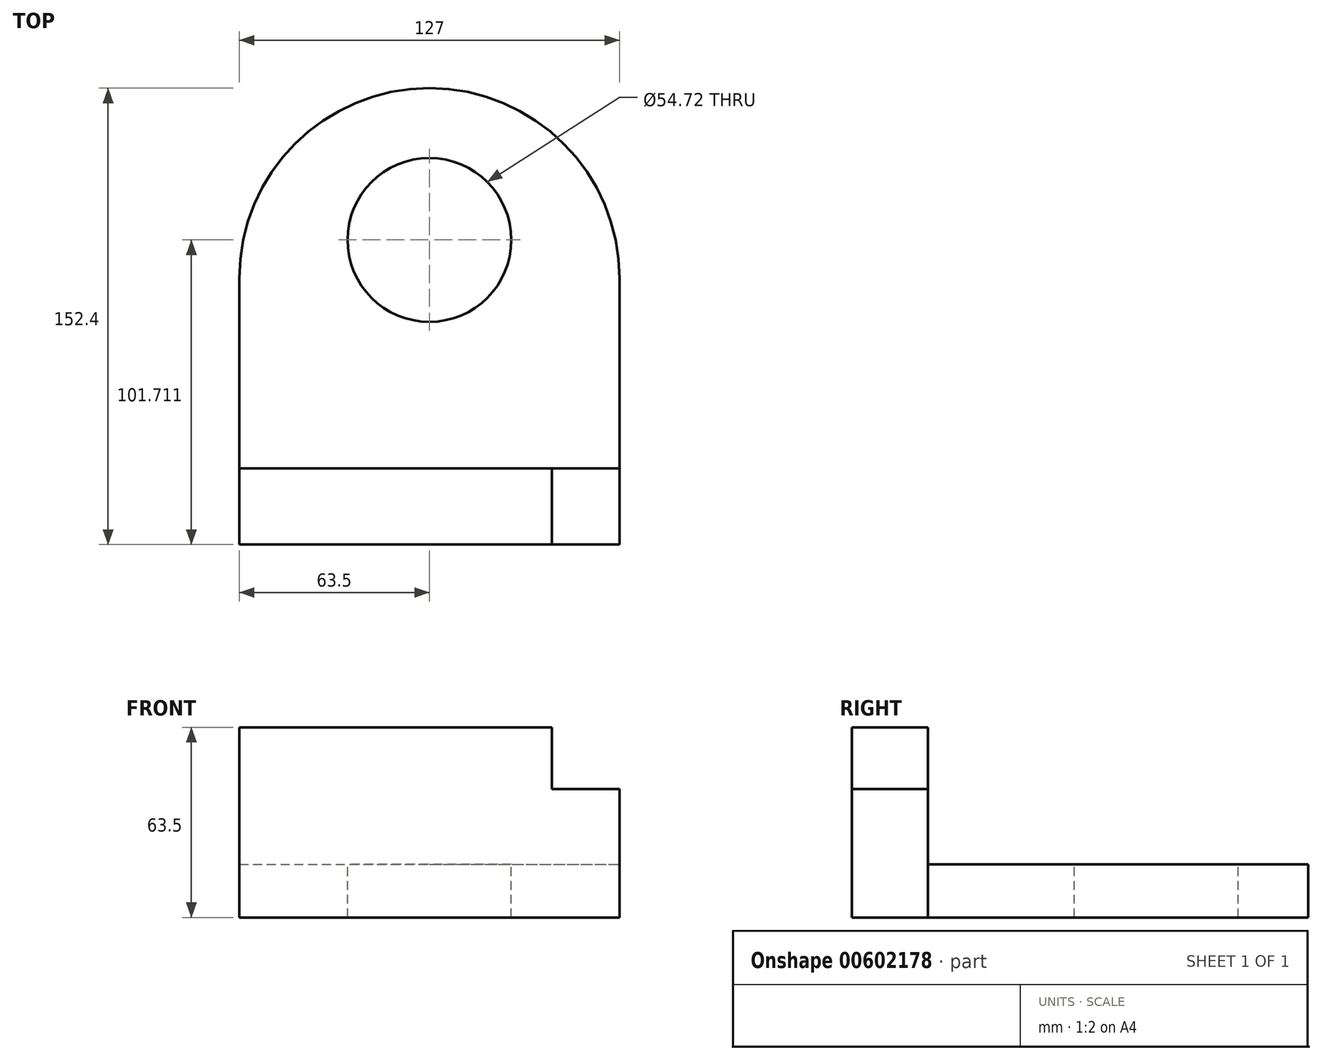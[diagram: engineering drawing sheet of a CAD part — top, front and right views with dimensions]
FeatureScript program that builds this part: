
annotation { "Feature Type Name" : "Feature", "Feature Type Description" : "" }
export const myFeature = defineFeature(function(context is Context, id is Id, definition is map)
    precondition{}
    {
        {
            var Q0;
            Q0=qCreatedBy(makeId("Front.planeOp"),FACE);
            var sketch = newSketch(context, id + "F0", { "sketchPlane" : qUnion([Q0])});
            skLineSegment(sketch, "E0.bottom", {"start": v(-63.5, 31.75) * mm, "end": v(63.5, 31.75) * mm});
            skLineSegment(sketch, "E0.top", {"start": v(-63.5, -31.75) * mm, "end": v(63.5, -31.75) * mm});
            skLineSegment(sketch, "E0.left", {"start": v(-63.5, 31.75) * mm, "end": v(-63.5, -31.75) * mm});
            skLineSegment(sketch, "E0.right", {"start": v(63.5, 31.75) * mm, "end": v(63.5, -31.75) * mm});
            skPoint(sketch, "E0.middle", {"position": v(0, 0) * mm});
            skSolve(sketch);
        }
        {
            var Q0;
            Q0=makeQuery(id+"F0.imprint","IMPRINT",FACE,{"disambiguationData":[TD([[makeQuery(id+"F0.imprint","IMPRINT",EDGE,{"derivedFrom":sQuery(id+"F0.wireOp",EDGE,"E0.bottom")}),-1.0]])]});
            extrude(context, id + "F1", {"entities" : qUnion([Q0]), "depth" : 25.4 * mm, "offsetDistance" : 25.4 * mm});
        }
        {
            var Q0;
            Q0=makeQuery(id+"F1.opExtrude","CAP_FACE",FACE,{"disambiguationData":[OSD([sQuery(id+"F0.wireOp",EDGE,"E0.bottom"),sQuery(id+"F0.wireOp",EDGE,"E0.top"),sQuery(id+"F0.wireOp",EDGE,"E0.left"),sQuery(id+"F0.wireOp",EDGE,"E0.right")])],"isStart":false});
            var sketch = newSketch(context, id + "F2", { "sketchPlane" : qUnion([Q0])});
            skLineSegment(sketch, "E1.bottom", {"start": v(63.5, 31.75) * mm, "end": v(40.95, 31.75) * mm});
            skLineSegment(sketch, "E1.top", {"start": v(63.5, 11.08) * mm, "end": v(40.95, 11.08) * mm});
            skLineSegment(sketch, "E1.left", {"start": v(63.5, 31.75) * mm, "end": v(63.5, 11.08) * mm});
            skLineSegment(sketch, "E1.right", {"start": v(40.95, 31.75) * mm, "end": v(40.95, 11.08) * mm});
            skSolve(sketch);
        }
        {
            var Q0;
            Q0=makeQuery(id+"F2.imprint","IMPRINT",FACE,{"disambiguationData":[TD([[makeQuery(id+"F2.imprint","IMPRINT",EDGE,{"derivedFrom":sQuery(id+"F2.wireOp",EDGE,"E1.bottom")}),-1.0]])]});
            extrude(context, id + "F3", {"entities" : qUnion([Q0]), "operationType" : NewBodyOperationType.REMOVE, "oppositeDirection" : true, "depth" : 25.4 * mm, "offsetDistance" : 25.4 * mm});
        }
        {
            var Q0;
            Q0=qCreatedBy(makeId("Front.planeOp"),FACE);
            var sketch = newSketch(context, id + "F4", { "sketchPlane" : qUnion([Q0])});
            skLineSegment(sketch, "E2.bottom", {"start": v(-63.5, -13.97) * mm, "end": v(63.5, -13.97) * mm});
            skLineSegment(sketch, "E2.top", {"start": v(-63.5, -31.75) * mm, "end": v(63.5, -31.75) * mm});
            skLineSegment(sketch, "E2.left", {"start": v(-63.5, -13.97) * mm, "end": v(-63.5, -31.75) * mm});
            skLineSegment(sketch, "E2.right", {"start": v(63.5, -13.97) * mm, "end": v(63.5, -31.75) * mm});
            skSolve(sketch);
        }
        {
            var Q0;
            Q0=makeQuery(id+"F4.imprint","IMPRINT",FACE,{"disambiguationData":[TD([[makeQuery(id+"F4.imprint","IMPRINT",EDGE,{"derivedFrom":sQuery(id+"F4.wireOp",EDGE,"E2.bottom")}),-1.0]])]});
            extrude(context, id + "F5", {"entities" : qUnion([Q0]), "oppositeDirection" : true, "depth" : 127 * mm, "offsetDistance" : 25.4 * mm});
        }
        {
            var Q0;
            Q0=makeQuery(id+"F5.opExtrude","CAP_EDGE",EDGE,{"disambiguationData":[OSD([sQuery(id+"F4.wireOp",EDGE,"E2.right")])],"isStart":false});
            fillet(context, id + "F6", {"entities" : qUnion([Q0]), "radius" : 63.5 * mm, "tangentPropagation" : true, "allowEdgeOverflow" : false});
        }
        {
            var Q0;
            Q0=makeQuery(id+"F5.opExtrude","CAP_EDGE",EDGE,{"disambiguationData":[OSD([sQuery(id+"F4.wireOp",EDGE,"E2.left")])],"isStart":false});
            fillet(context, id + "F7", {"entities" : qUnion([Q0]), "radius" : 63.5 * mm, "tangentPropagation" : true, "allowEdgeOverflow" : false});
        }
        {
            var Q0;
            Q0=makeQuery(id+"F5.opExtrude","SWEPT_FACE",FACE,{"disambiguationData":[OSD([sQuery(id+"F4.wireOp",EDGE,"E2.bottom")])]});
            var sketch = newSketch(context, id + "F8", { "sketchPlane" : qUnion([Q0])});
            skCircle(sketch, "E3", {"center": v(0, 76.31) * mm, "radius": 27.36 * mm});
            skSolve(sketch);
        }
        {
            var Q0;
            Q0=makeQuery(id+"F8.imprint","IMPRINT",FACE,{"disambiguationData":[TD([[makeQuery(id+"F8.imprint","IMPRINT",EDGE,{"derivedFrom":sQuery(id+"F8.wireOp",EDGE,"E3")}),1.0]])]});
            extrude(context, id + "F9", {"entities" : qUnion([Q0]), "operationType" : NewBodyOperationType.REMOVE, "oppositeDirection" : true, "depth" : 25.4 * mm, "offsetDistance" : 25.4 * mm});
        }
    });
